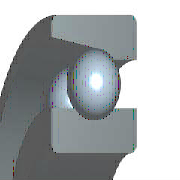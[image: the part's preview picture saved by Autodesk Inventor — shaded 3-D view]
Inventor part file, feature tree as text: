
AUTODESK INVENTOR PART (.ipt)
format: ipt  version: 2025.2 (Build 292293000, 293)  size: 298,496 bytes
history: native  units: mm (DEFAULTED — no unit token found)
features: other x2, pattern_circular x1
ambient origin geometry x8: Origin, YZ Plane, XZ Plane, XY Plane, X Axis, Y Axis, Z Axis, Center Point
bodies: Solid1 (feature_tree)
feature tree (3):
  other  "Körper"
  other  "Kugel"
  pattern_circular  "Kugeln"  [2 undecoded]
note: 2 required parameter values undecoded (feature->parameter linkage not recoverable at this tier; creation-order binding heuristic only, values carry confidence <= 0.55)
